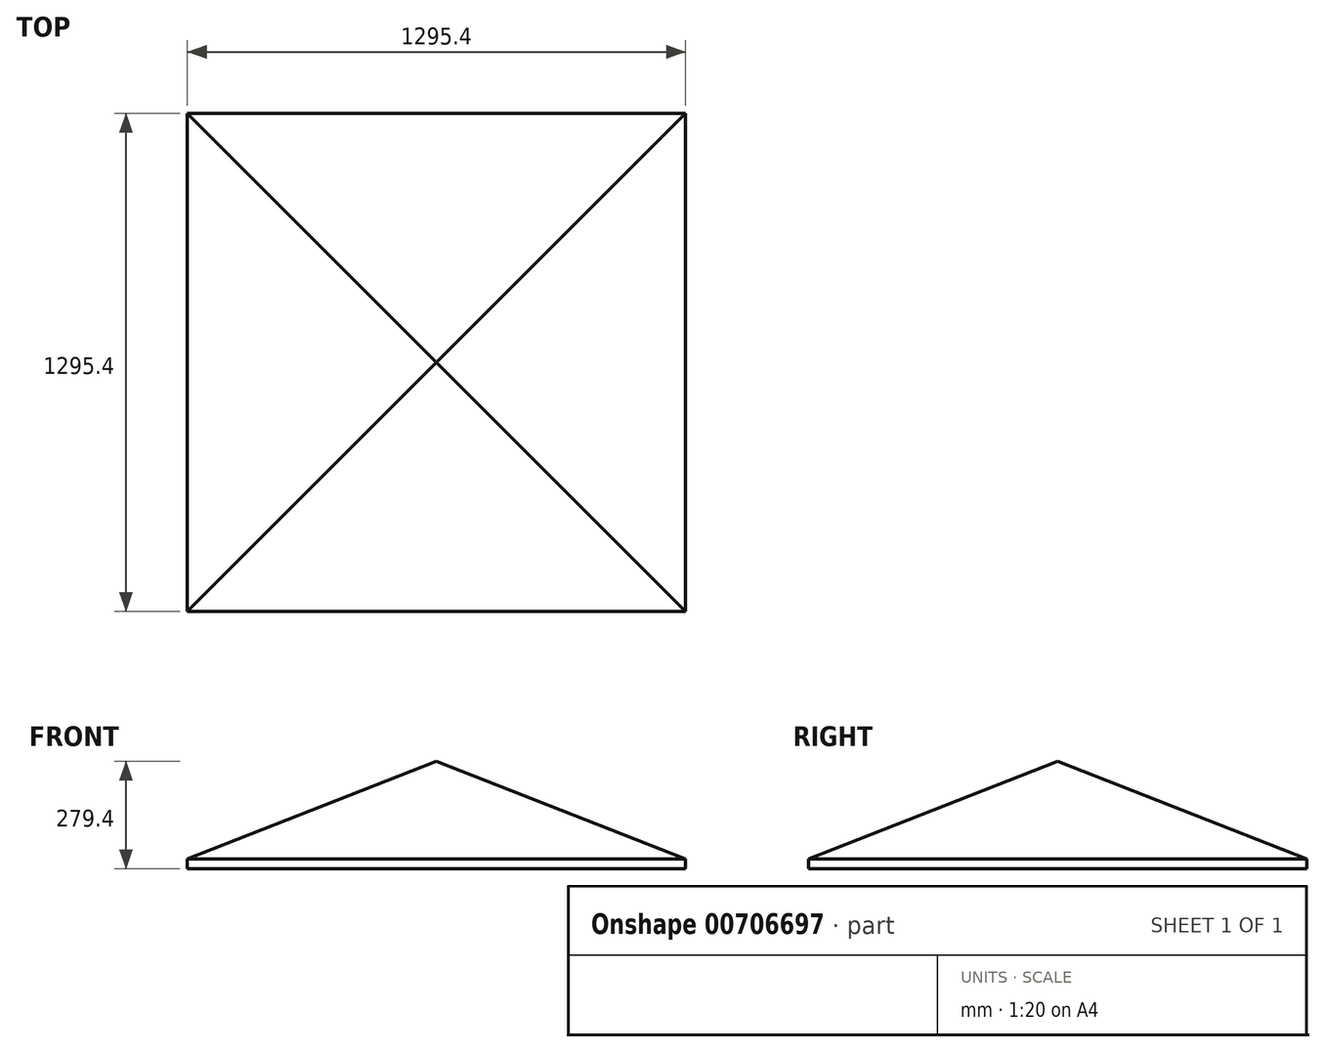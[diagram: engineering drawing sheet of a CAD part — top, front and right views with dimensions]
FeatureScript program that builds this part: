
annotation { "Feature Type Name" : "Feature", "Feature Type Description" : "" }
export const myFeature = defineFeature(function(context is Context, id is Id, definition is map)
    precondition{}
    {
        {
            var Q0;
            Q0=qCreatedBy(makeId("Top.planeOp"),FACE);
            var sketch = newSketch(context, id + "F0", { "sketchPlane" : qUnion([Q0])});
            skLineSegment(sketch, "E0.bottom", {"start": v(0, 0) * mm, "end": v(647.7, 0) * mm});
            skLineSegment(sketch, "E0.top", {"start": v(0, 647.7) * mm, "end": v(647.7, 647.7) * mm});
            skLineSegment(sketch, "E0.left", {"start": v(0, 0) * mm, "end": v(0, 647.7) * mm});
            skLineSegment(sketch, "E0.right", {"start": v(647.7, 0) * mm, "end": v(647.7, 647.7) * mm});
            skLineSegment(sketch, "E1.bottom", {"start": v(0, 0) * mm, "end": v(-647.7, 0) * mm});
            skLineSegment(sketch, "E1.top", {"start": v(0, 647.7) * mm, "end": v(-647.7, 647.7) * mm});
            skLineSegment(sketch, "E1.right", {"start": v(-647.7, 0) * mm, "end": v(-647.7, 647.7) * mm});
            skLineSegment(sketch, "E2.top", {"start": v(0, -647.7) * mm, "end": v(-647.7, -647.7) * mm});
            skLineSegment(sketch, "E2.left", {"start": v(0, 0) * mm, "end": v(0, -647.7) * mm});
            skLineSegment(sketch, "E2.right", {"start": v(-647.7, 0) * mm, "end": v(-647.7, -647.7) * mm});
            skLineSegment(sketch, "E3.top", {"start": v(0, -647.7) * mm, "end": v(647.7, -647.7) * mm});
            skLineSegment(sketch, "E3.right", {"start": v(647.7, 0) * mm, "end": v(647.7, -647.7) * mm});
            skSolve(sketch);
        }
        {
            var Q0;
            Q0=makeQuery(id+"F0.imprint","IMPRINT",FACE,{"disambiguationData":[TD([[makeQuery(id+"F0.imprint","IMPRINT",EDGE,{"derivedFrom":sQuery(id+"F0.wireOp",EDGE,"E0.top")}),-1.0]])]});
            var Q1;
            Q1=makeQuery(id+"F0.imprint","IMPRINT",FACE,{"disambiguationData":[TD([[makeQuery(id+"F0.imprint","IMPRINT",EDGE,{"derivedFrom":sQuery(id+"F0.wireOp",EDGE,"E1.top")}),1.0]])]});
            var Q2;
            Q2=makeQuery(id+"F0.imprint","IMPRINT",FACE,{"disambiguationData":[TD([[makeQuery(id+"F0.imprint","IMPRINT",EDGE,{"derivedFrom":sQuery(id+"F0.wireOp",EDGE,"E1.bottom")}),1.0]])]});
            var Q3;
            Q3=makeQuery(id+"F0.imprint","IMPRINT",FACE,{"disambiguationData":[TD([[makeQuery(id+"F0.imprint","IMPRINT",EDGE,{"derivedFrom":sQuery(id+"F0.wireOp",EDGE,"E0.bottom")}),-1.0]])]});
            extrude(context, id + "F1", {"entities" : qUnion([Q0, Q1, Q2, Q3]), "depth" : -25.4 * mm, "offsetDistance" : 25.4 * mm});
        }
        {
            var Q0;
            Q0=qCreatedBy(makeId("Front.planeOp"),FACE);
            var sketch = newSketch(context, id + "F2", { "sketchPlane" : qUnion([Q0])});
            skLineSegment(sketch, "E4", {"start": v(0, 0) * mm, "end": v(0, 254) * mm});
            skSolve(sketch);
        }
        {
            var Q1;
            Q1=sQuery(id+"F2.wireOp",VERTEX,"E4.end");
            var Q2;
            Q2=makeQuery(id+"F1.opExtrude","CAP_FACE",FACE,{"disambiguationData":[OSD([sQuery(id+"F0.wireOp",EDGE,"E0.top"),sQuery(id+"F0.wireOp",EDGE,"E0.right"),sQuery(id+"F0.wireOp",EDGE,"E1.top"),sQuery(id+"F0.wireOp",EDGE,"E1.right"),sQuery(id+"F0.wireOp",EDGE,"E2.top"),sQuery(id+"F0.wireOp",EDGE,"E2.right"),sQuery(id+"F0.wireOp",EDGE,"E3.top"),sQuery(id+"F0.wireOp",EDGE,"E3.right")])],"isStart":true});
            loft(context, id + "F3", {"operationType" : NewBodyOperationType.ADD, "sheetProfilesArray" : [{ "sheetProfileEntities" : qUnion([Q1]) }, { "sheetProfileEntities" : qUnion([Q2]) }]});
        }
    });
